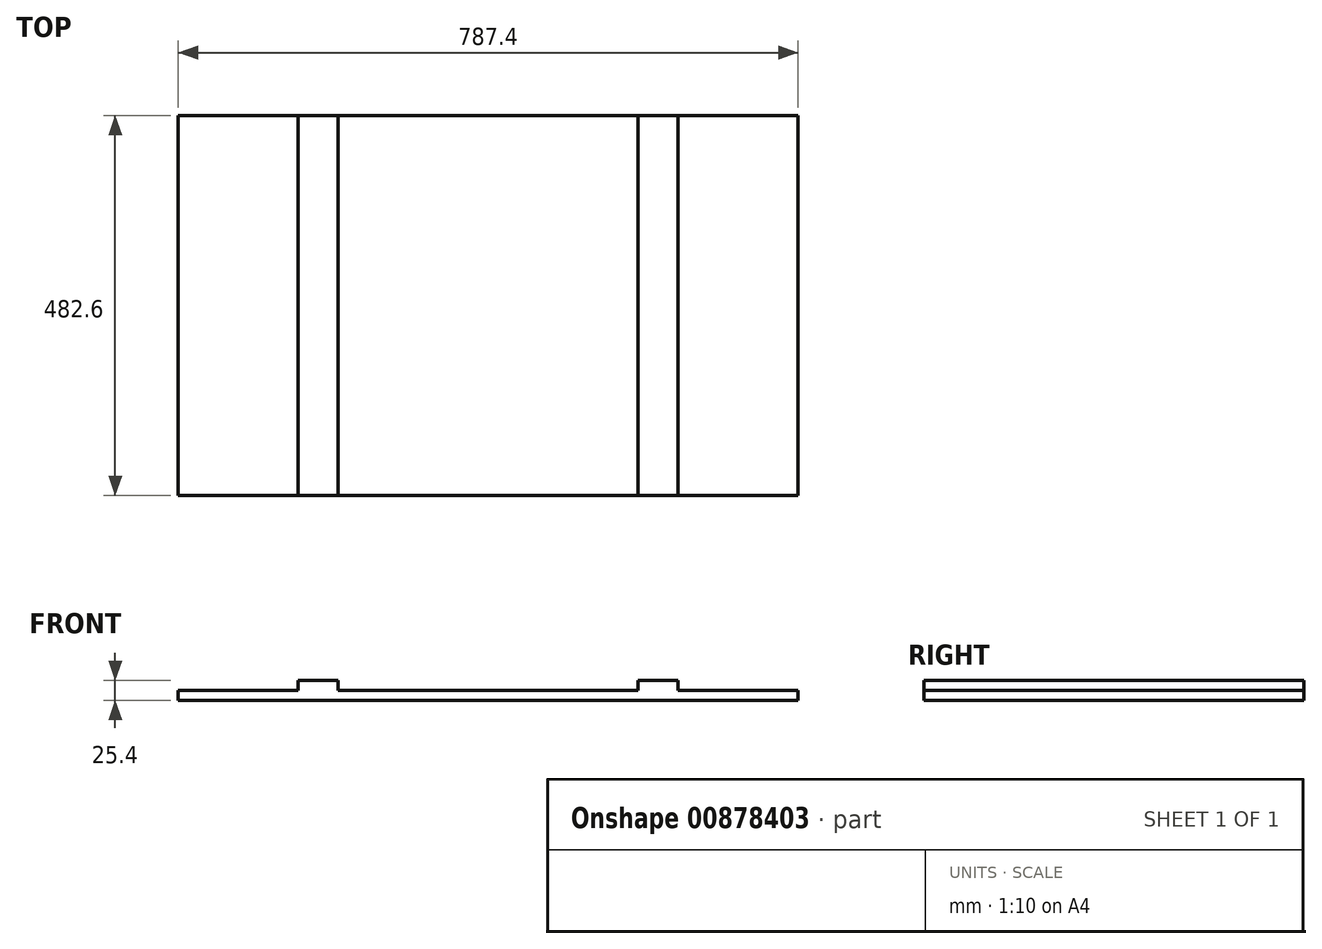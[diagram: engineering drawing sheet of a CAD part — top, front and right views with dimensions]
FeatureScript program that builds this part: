
annotation { "Feature Type Name" : "Feature", "Feature Type Description" : "" }
export const myFeature = defineFeature(function(context is Context, id is Id, definition is map)
    precondition{}
    {
        {
            var Q0;
            Q0=qCreatedBy(makeId("Top.planeOp"),FACE);
            var sketch = newSketch(context, id + "F0", { "sketchPlane" : qUnion([Q0])});
            skLineSegment(sketch, "E0.bottom", {"start": v(0, 0) * mm, "end": v(787.4, 0) * mm});
            skLineSegment(sketch, "E0.top", {"start": v(0, 482.6) * mm, "end": v(787.4, 482.6) * mm});
            skLineSegment(sketch, "E0.left", {"start": v(0, 0) * mm, "end": v(0, 482.6) * mm});
            skLineSegment(sketch, "E0.right", {"start": v(787.4, 0) * mm, "end": v(787.4, 482.6) * mm});
            skSolve(sketch);
        }
        {
            var Q0;
            Q0=makeQuery(id+"F0.imprint","IMPRINT",FACE,{"disambiguationData":[TD([[makeQuery(id+"F0.imprint","IMPRINT",EDGE,{"derivedFrom":sQuery(id+"F0.wireOp",EDGE,"E0.bottom")}),1.0]])]});
            extrude(context, id + "F1", {"entities" : qUnion([Q0]), "depth" : 12.7 * mm, "offsetDistance" : 25.4 * mm});
        }
        {
            var Q0;
            Q0=makeQuery(id+"F1.opExtrude","CAP_FACE",FACE,{"disambiguationData":[OSD([sQuery(id+"F0.wireOp",EDGE,"E0.bottom"),sQuery(id+"F0.wireOp",EDGE,"E0.top"),sQuery(id+"F0.wireOp",EDGE,"E0.left"),sQuery(id+"F0.wireOp",EDGE,"E0.right")])],"isStart":false});
            var sketch = newSketch(context, id + "F2", { "sketchPlane" : qUnion([Q0])});
            skLineSegment(sketch, "E1.bottom", {"start": v(152.4, 482.6) * mm, "end": v(203.2, 482.6) * mm});
            skLineSegment(sketch, "E1.top", {"start": v(152.4, 0) * mm, "end": v(203.2, 0) * mm});
            skLineSegment(sketch, "E1.left", {"start": v(152.4, 482.6) * mm, "end": v(152.4, 0) * mm});
            skLineSegment(sketch, "E1.right", {"start": v(203.2, 482.6) * mm, "end": v(203.2, 0) * mm});
            skLineSegment(sketch, "E2.bottom", {"start": v(635, 482.6) * mm, "end": v(584.2, 482.6) * mm});
            skLineSegment(sketch, "E2.top", {"start": v(635, 0) * mm, "end": v(584.2, 0) * mm});
            skLineSegment(sketch, "E2.left", {"start": v(635, 482.6) * mm, "end": v(635, 0) * mm});
            skLineSegment(sketch, "E2.right", {"start": v(584.2, 482.6) * mm, "end": v(584.2, 0) * mm});
            skSolve(sketch);
        }
        {
            var Q0;
            Q0 = qSketchRegion(id + "F2", true);
            extrude(context, id + "F3", {"entities" : qUnion([Q0]), "operationType" : NewBodyOperationType.ADD, "depth" : 12.7 * mm, "offsetDistance" : 25.4 * mm});
        }
    });
